# Revit family: Porecz_uchylna_dla_niepelnosprawnych_600 mm stal szlachetna matowa
name_source: partatom
category: Furniture
units: mm (PartAtom-declared; Revit-internal decimal feet)

## family parameters
Always vertical = Yes
Cut with Voids When Loaded = No
Host = Wall
Room Calculation Point = No
Shared = No

## types (1)
- S32UUWC8SNM
    Depth / Glebokosc = 600 mm
    Description = Poręcz uchylna dla niepełnosprawnych o długości 60 cm wyprodukowana jest ze stali nierdzewnej o matowym wykończeniu. To prosty w montażu i łatwy w czyszczeniu oraz konserwacji pochwyt łazienkowy, mocowany w toaletach publicznych, z których korzystają osoby z problemami ruchowymi. Głównym zadaniem poręczy jest ich asekuracja podczas wykonywania wszelkich czynności w toalecie, co zwiększa  bezpieczeństwo i komfort użytkowników. Odchylany do góry uchwyt wyposażony jest w progresywny system hamulcowy, który zabezpiecza go przed nagłym opadnięciem. Stalowy pochwyt polecany jest do szpitali, szkół, hoteli, domów opieki oraz sanatoriów.
    Height / Wysokosc = 250 mm  [stored 0.82021 ft]
    Manufacturer = FANECO.com
    Manufacturer code / Kod producenta = 5901764294924
    Material = Stal nierdzewna AISI 316
    Material finish / Wykonczenie = Stal nierdzewna AISI 316
    Product code / Kod produktu = S32UUWC6SNM
    Type Comments = Poręcz uchylna dla niepełnosprawnych 600 mm stal szlachetna matowa
    URL = https://faneco.com
    Weight / Waga = 2.6 kg
    Width / Szerokosc = 120 mm  [stored 0.393701 ft]

note: [stored X ft] marks values corroborated as IEEE doubles in the binary element streams (Revit-internal decimal feet)

## geometry (parser evidence)
native form markers: Sweep x8
no freeform markers — native parametric forms only
